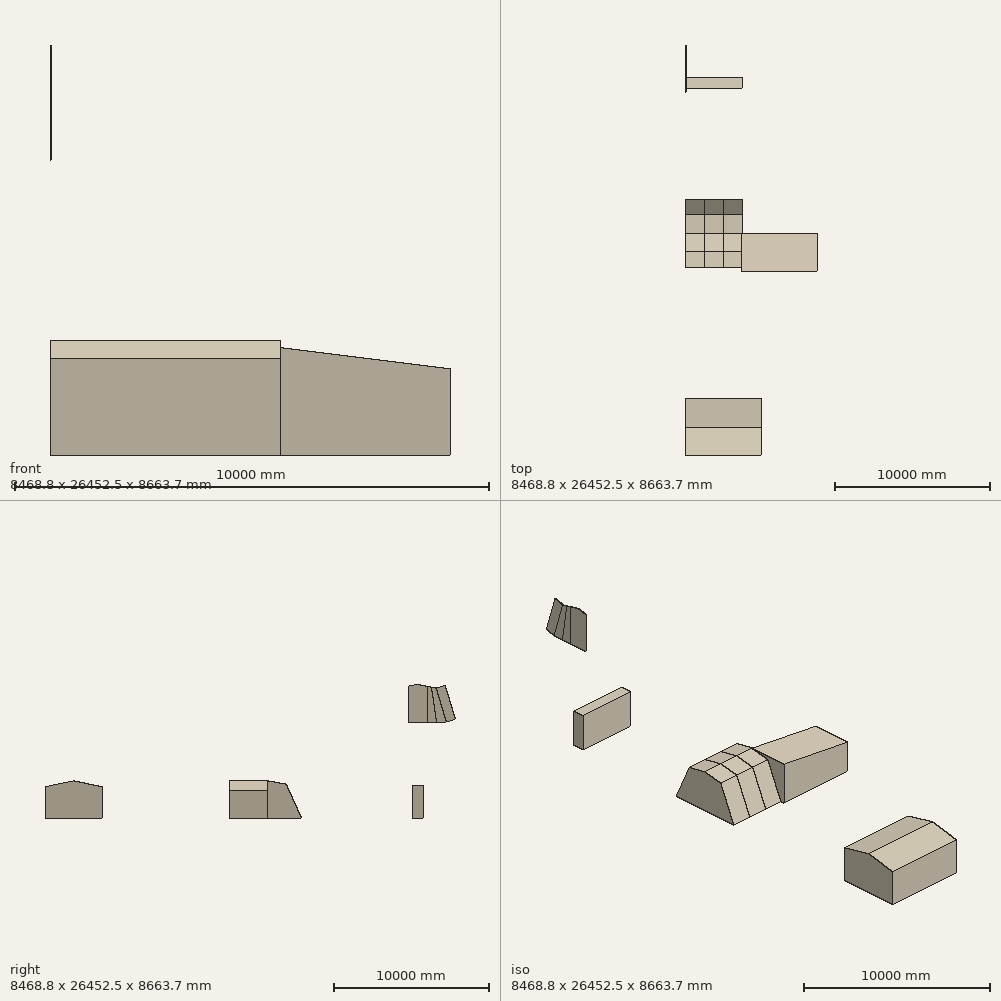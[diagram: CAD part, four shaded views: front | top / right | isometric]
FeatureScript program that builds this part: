
annotation { "Feature Type Name" : "Feature", "Feature Type Description" : "" }
export const myFeature = defineFeature(function(context is Context, id is Id, definition is map)
    precondition{}
    {
        {
            var Q0;
            Q0=qCreatedBy(makeId("Front.planeOp"),FACE);
            var sketch = newSketch(context, id + "F0", { "sketchPlane" : qUnion([Q0])});
            skLineSegment(sketch, "E0", {"start": v(3591.95, 0) * mm, "end": v(3591.95, 2438.4) * mm});
            skLineSegment(sketch, "E1", {"start": v(3591.95, 2438.4) * mm, "end": v(8468.75, 1828.8) * mm});
            skLineSegment(sketch, "E2", {"start": v(8468.75, 1828.8) * mm, "end": v(8468.75, 0) * mm});
            skLineSegment(sketch, "E3", {"start": v(8468.75, 0) * mm, "end": v(3591.95, 0) * mm});
            skSolve(sketch);
        }
        {
            var Q0;
            Q0=makeQuery(id+"F0.imprint","IMPRINT",FACE,{"disambiguationData":[TD([[makeQuery(id+"F0.imprint","IMPRINT",EDGE,{"derivedFrom":sQuery(id+"F0.wireOp",EDGE,"E0")}),-1.0]])]});
            extrude(context, id + "F1", {"entities" : qUnion([Q0]), "depth" : 2438.4 * mm});
        }
        {
            var Q0;
            Q0=qCreatedBy(makeId("Right.planeOp"),FACE);
            var sketch = newSketch(context, id + "F2", { "sketchPlane" : qUnion([Q0])});
            skLineSegment(sketch, "E4", {"start": v(-14333.51, 0) * mm, "end": v(-10675.91, 0) * mm});
            skLineSegment(sketch, "E5", {"start": v(-10675.91, 0) * mm, "end": v(-10675.91, 2057.4) * mm});
            skLineSegment(sketch, "E6", {"start": v(-10675.91, 2057.4) * mm, "end": v(-12504.71, 2438.4) * mm});
            skLineSegment(sketch, "E7", {"start": v(-12504.71, 2438.4) * mm, "end": v(-14333.51, 2057.4) * mm});
            skLineSegment(sketch, "E8", {"start": v(-14333.51, 2057.4) * mm, "end": v(-14333.51, 0) * mm});
            skLineSegment(sketch, "E9", {"start": v(2202.6, 0) * mm, "end": v(0, 0) * mm});
            skLineSegment(sketch, "E10", {"start": v(0, 0) * mm, "end": v(0, 2438.4) * mm, "construction": true});
            skLineSegment(sketch, "E11", {"start": v(0, 2438.4) * mm, "end": v(1199.97, 2222.73) * mm});
            skLineSegment(sketch, "E12", {"start": v(1199.97, 2222.73) * mm, "end": v(2202.6, 0) * mm});
            skLineSegment(sketch, "E13", {"start": v(711.2, 0) * mm, "end": v(711.2, 2310.57) * mm, "construction": true});
            skLineSegment(sketch, "E14", {"start": v(711.2, 2310.57) * mm, "end": v(711.2, 3306.28) * mm, "construction": true});
            skLineSegment(sketch, "E15", {"start": v(711.2, 3306.28) * mm, "end": v(1199.97, 2222.73) * mm, "construction": true});
            skLineSegment(sketch, "E16", {"start": v(711.2, 3306.28) * mm, "end": v(1422.4, 0) * mm, "construction": true});
            skLineSegment(sketch, "E17", {"start": v(711.2, 3306.28) * mm, "end": v(711.2, 3306.28) * mm});
            skLineSegment(sketch, "E18", {"start": v(1390.95, 146.22) * mm, "end": v(711.2, 0) * mm, "construction": true});
            skLineSegment(sketch, "E19", {"start": v(2070.7, 292.44) * mm, "end": v(1422.4, 0) * mm, "construction": true});
            skLineSegment(sketch, "E20", {"start": v(1390.95, 146.22) * mm, "end": v(711.2, 146.22) * mm, "construction": true});
            skLineSegment(sketch, "E21", {"start": v(2202.6, 5599.6) * mm, "end": v(0, 5599.6) * mm});
            skLineSegment(sketch, "E22", {"start": v(0, 5599.6) * mm, "end": v(0, 8038) * mm});
            skLineSegment(sketch, "E23", {"start": v(0, 8038) * mm, "end": v(1199.97, 7822.32) * mm});
            skLineSegment(sketch, "E24", {"start": v(1199.97, 7822.32) * mm, "end": v(2202.6, 5599.6) * mm});
            skLineSegment(sketch, "E25", {"start": v(711.2, 5599.6) * mm, "end": v(711.2, 7910.17) * mm});
            skLineSegment(sketch, "E26", {"start": v(711.2, 7910.17) * mm, "end": v(711.2, 8905.88) * mm, "construction": true});
            skLineSegment(sketch, "E27", {"start": v(711.2, 8905.88) * mm, "end": v(1199.97, 7822.32) * mm, "construction": true});
            skLineSegment(sketch, "E28", {"start": v(711.2, 8905.88) * mm, "end": v(1422.4, 5599.6) * mm, "construction": true});
            skLineSegment(sketch, "E29", {"start": v(711.2, 8905.88) * mm, "end": v(711.2, 8905.88) * mm});
            skLineSegment(sketch, "E30", {"start": v(1390.95, 5745.82) * mm, "end": v(711.2, 5599.6) * mm, "construction": true});
            skLineSegment(sketch, "E31", {"start": v(2070.7, 5892.03) * mm, "end": v(1422.4, 5599.6) * mm, "construction": true});
            skLineSegment(sketch, "E32", {"start": v(1390.95, 5745.82) * mm, "end": v(711.2, 5745.82) * mm, "construction": true});
            skLineSegment(sketch, "E33.MirrorCS", {"start": v(711.2, 8905.88) * mm, "end": v(0, 5599.6) * mm, "construction": true});
            skLineSegment(sketch, "E34", {"start": v(2070.7, 5892.03) * mm, "end": v(2202.6, 5599.6) * mm});
            skLineSegment(sketch, "E35", {"start": v(711.2, 5599.6) * mm, "end": v(711.2, 5278.79) * mm});
            skLineSegment(sketch, "E36", {"start": v(711.2, 5278.79) * mm, "end": v(0, 5599.6) * mm});
            skLineSegment(sketch, "E37", {"start": v(711.2, 7910.17) * mm, "end": v(934, 7870.13) * mm});
            skLineSegment(sketch, "E38.MirrorCS", {"start": v(711.2, 7910.17) * mm, "end": v(488.4, 7870.13) * mm});
            skLineSegment(sketch, "E39.left", {"start": v(711.2, 5278.79) * mm, "end": v(711.2, 7717.19) * mm});
            skLineSegment(sketch, "E40", {"start": v(711.2, 7717.19) * mm, "end": v(488.4, 7870.13) * mm});
            skLineSegment(sketch, "E41", {"start": v(488.4, 7870.13) * mm, "end": v(0, 5599.6) * mm});
            skLineSegment(sketch, "E42.MirrorCS", {"start": v(-711.2, 0) * mm, "end": v(-711.2, 2310.57) * mm, "construction": true});
            skLineSegment(sketch, "E43.MirrorCS", {"start": v(-2202.6, 0) * mm, "end": v(0, 0) * mm});
            skLineSegment(sketch, "E44.MirrorCS", {"start": v(-1390.95, 146.22) * mm, "end": v(-711.2, 0) * mm, "construction": true});
            skLineSegment(sketch, "E45.MirrorCS", {"start": v(-711.2, 3306.28) * mm, "end": v(-1422.4, 0) * mm, "construction": true});
            skLineSegment(sketch, "E46.MirrorCS", {"start": v(-711.2, 3306.28) * mm, "end": v(-1199.97, 2222.73) * mm, "construction": true});
            skLineSegment(sketch, "E47.MirrorCS", {"start": v(-1390.95, 146.22) * mm, "end": v(-711.2, 146.22) * mm, "construction": true});
            skLineSegment(sketch, "E48.MirrorCS", {"start": v(-1199.97, 2222.73) * mm, "end": v(-2202.6, 0) * mm});
            skLineSegment(sketch, "E49.MirrorCS", {"start": v(0, 2438.4) * mm, "end": v(-1199.97, 2222.73) * mm});
            skLineSegment(sketch, "E50.MirrorCS", {"start": v(-711.2, 2310.57) * mm, "end": v(-711.2, 3306.28) * mm, "construction": true});
            skLineSegment(sketch, "E51.MirrorCS", {"start": v(-2070.7, 292.44) * mm, "end": v(-1422.4, 0) * mm, "construction": true});
            skLineSegment(sketch, "E52.bottom", {"start": v(711.2, 5278.79) * mm, "end": v(101.6, 5278.79) * mm});
            skLineSegment(sketch, "E52.top", {"start": v(711.2, 7717.19) * mm, "end": v(101.6, 7717.19) * mm});
            skLineSegment(sketch, "E52.right", {"start": v(101.6, 5278.79) * mm, "end": v(101.6, 7717.19) * mm});
            skLineSegment(sketch, "E53", {"start": v(609.6, 0) * mm, "end": v(609.6, 2328.84) * mm, "construction": true});
            skLineSegment(sketch, "E54.MirrorCS", {"start": v(-609.6, 0) * mm, "end": v(-609.6, 2328.84) * mm, "construction": true});
            skLineSegment(sketch, "E55", {"start": v(11535.56, 0) * mm, "end": v(9679.38, 0) * mm});
            skLineSegment(sketch, "E56", {"start": v(9679.38, 0) * mm, "end": v(9679.38, 2438.4) * mm, "construction": true});
            skLineSegment(sketch, "E57", {"start": v(9679.38, 2438.4) * mm, "end": v(10872.53, 2187.74) * mm});
            skLineSegment(sketch, "E58", {"start": v(10872.53, 2187.74) * mm, "end": v(11535.56, 0) * mm});
            skLineSegment(sketch, "E59", {"start": v(10288.98, 0) * mm, "end": v(10288.98, 2310.33) * mm, "construction": true});
            skLineSegment(sketch, "E60", {"start": v(10288.98, 2310.33) * mm, "end": v(10288.98, 4113.24) * mm, "construction": true});
            skLineSegment(sketch, "E61", {"start": v(10288.98, 4113.24) * mm, "end": v(10872.53, 2187.74) * mm, "construction": true});
            skLineSegment(sketch, "E62", {"start": v(10288.98, 4113.24) * mm, "end": v(10898.58, 0) * mm, "construction": true});
            skLineSegment(sketch, "E63", {"start": v(10288.98, 4113.24) * mm, "end": v(10288.98, 4113.24) * mm});
            skLineSegment(sketch, "E64", {"start": v(10885.48, 88.4) * mm, "end": v(10288.98, 0) * mm, "construction": true});
            skLineSegment(sketch, "E65", {"start": v(11481.97, 176.8) * mm, "end": v(10898.58, 0) * mm, "construction": true});
            skLineSegment(sketch, "E66", {"start": v(10885.48, 88.4) * mm, "end": v(10288.98, 88.4) * mm, "construction": true});
            skLineSegment(sketch, "E67.MirrorCS", {"start": v(9069.78, 0) * mm, "end": v(9069.78, 2310.33) * mm, "construction": true});
            skLineSegment(sketch, "E68.MirrorCS", {"start": v(7823.2, 0) * mm, "end": v(9679.38, 0) * mm});
            skLineSegment(sketch, "E69.MirrorCS", {"start": v(8473.28, 88.4) * mm, "end": v(9069.78, 0) * mm, "construction": true});
            skLineSegment(sketch, "E70.MirrorCS", {"start": v(9069.78, 4113.24) * mm, "end": v(8460.18, 0) * mm, "construction": true});
            skLineSegment(sketch, "E71.MirrorCS", {"start": v(9069.78, 4113.24) * mm, "end": v(8486.22, 2187.74) * mm, "construction": true});
            skLineSegment(sketch, "E72.MirrorCS", {"start": v(8473.28, 88.4) * mm, "end": v(9069.78, 88.4) * mm, "construction": true});
            skLineSegment(sketch, "E73.MirrorCS", {"start": v(8486.22, 2187.74) * mm, "end": v(7823.2, 0) * mm});
            skLineSegment(sketch, "E74.MirrorCS", {"start": v(9679.38, 2438.4) * mm, "end": v(8486.22, 2187.74) * mm});
            skLineSegment(sketch, "E75.MirrorCS", {"start": v(9069.78, 2310.33) * mm, "end": v(9069.78, 4113.24) * mm, "construction": true});
            skLineSegment(sketch, "E76.MirrorCS", {"start": v(7876.78, 176.8) * mm, "end": v(8460.18, 0) * mm, "construction": true});
            skLineSegment(sketch, "E77", {"start": v(11535.56, 6225.26) * mm, "end": v(9679.38, 6225.26) * mm});
            skLineSegment(sketch, "E78", {"start": v(9679.38, 6225.26) * mm, "end": v(9679.38, 8663.66) * mm, "construction": true});
            skLineSegment(sketch, "E79", {"start": v(9679.38, 8663.66) * mm, "end": v(10872.53, 8413) * mm});
            skLineSegment(sketch, "E80", {"start": v(10872.53, 8413) * mm, "end": v(11535.56, 6225.26) * mm});
            skLineSegment(sketch, "E81", {"start": v(10288.98, 6225.26) * mm, "end": v(10288.98, 8535.6) * mm, "construction": true});
            skLineSegment(sketch, "E82", {"start": v(10288.98, 8535.6) * mm, "end": v(10288.98, 10338.5) * mm, "construction": true});
            skLineSegment(sketch, "E83", {"start": v(10288.98, 10338.5) * mm, "end": v(10872.53, 8413) * mm, "construction": true});
            skLineSegment(sketch, "E84", {"start": v(10288.98, 10338.5) * mm, "end": v(10898.58, 6225.26) * mm, "construction": true});
            skLineSegment(sketch, "E85", {"start": v(10885.48, 6313.67) * mm, "end": v(10288.98, 6225.26) * mm, "construction": true});
            skLineSegment(sketch, "E86", {"start": v(11481.97, 6402.07) * mm, "end": v(10898.58, 6225.26) * mm, "construction": true});
            skLineSegment(sketch, "E87", {"start": v(10885.48, 6313.67) * mm, "end": v(10288.98, 6313.67) * mm, "construction": true});
            skLineSegment(sketch, "E88.MirrorCS", {"start": v(9069.78, 6225.26) * mm, "end": v(9069.78, 8535.6) * mm, "construction": true});
            skLineSegment(sketch, "E89.MirrorCS", {"start": v(7823.2, 6225.26) * mm, "end": v(9679.38, 6225.26) * mm});
            skLineSegment(sketch, "E90.MirrorCS", {"start": v(8473.28, 6313.67) * mm, "end": v(9069.78, 6225.26) * mm, "construction": true});
            skLineSegment(sketch, "E91.MirrorCS", {"start": v(9069.78, 10338.5) * mm, "end": v(8460.18, 6225.26) * mm, "construction": true});
            skLineSegment(sketch, "E92.MirrorCS", {"start": v(9069.78, 10338.5) * mm, "end": v(8486.22, 8413) * mm, "construction": true});
            skLineSegment(sketch, "E93.MirrorCS", {"start": v(8473.28, 6313.67) * mm, "end": v(9069.78, 6313.67) * mm, "construction": true});
            skLineSegment(sketch, "E94.MirrorCS", {"start": v(8486.22, 8413) * mm, "end": v(7823.2, 6225.26) * mm});
            skLineSegment(sketch, "E95.MirrorCS", {"start": v(9679.38, 8663.66) * mm, "end": v(8486.22, 8413) * mm});
            skLineSegment(sketch, "E96.MirrorCS", {"start": v(9069.78, 8535.6) * mm, "end": v(9069.78, 10338.5) * mm, "construction": true});
            skLineSegment(sketch, "E97.MirrorCS", {"start": v(7876.78, 6402.07) * mm, "end": v(8460.18, 6225.26) * mm, "construction": true});
            skLineSegment(sketch, "E98", {"start": v(10288.98, 8535.6) * mm, "end": v(10564.76, 8477.66) * mm});
            skLineSegment(sketch, "E99", {"start": v(10564.76, 8477.66) * mm, "end": v(10872.53, 8413) * mm});
            skLineSegment(sketch, "E100.MirrorCS", {"start": v(10288.98, 10338.5) * mm, "end": v(9679.38, 6225.26) * mm, "construction": true});
            skLineSegment(sketch, "E101.MirrorCS", {"start": v(10288.98, 8535.6) * mm, "end": v(10013.2, 8477.66) * mm});
            skLineSegment(sketch, "E102", {"start": v(10013.2, 8477.66) * mm, "end": v(10288.98, 8326.52) * mm});
            skLineSegment(sketch, "E103.bottom", {"start": v(10288.98, 8326.52) * mm, "end": v(9679.38, 8326.52) * mm});
            skLineSegment(sketch, "E103.top", {"start": v(10288.98, 6040.52) * mm, "end": v(9679.38, 6040.52) * mm});
            skLineSegment(sketch, "E103.left", {"start": v(10288.98, 8326.52) * mm, "end": v(10288.98, 6040.52) * mm});
            skLineSegment(sketch, "E103.right", {"start": v(9679.38, 8326.52) * mm, "end": v(9679.38, 6040.52) * mm});
            skLineSegment(sketch, "E104", {"start": v(10013.2, 8477.66) * mm, "end": v(9679.38, 6225.26) * mm});
            skLineSegment(sketch, "E105", {"start": v(9679.38, 6225.26) * mm, "end": v(10288.98, 6040.52) * mm});
            skLineSegment(sketch, "E106", {"start": v(9069.78, 8535.6) * mm, "end": v(9069.78, 6225.26) * mm});
            skLineSegment(sketch, "E107", {"start": v(10564.76, 8477.66) * mm, "end": v(10898.58, 6225.26) * mm});
            skLineSegment(sketch, "E108", {"start": v(11535.56, 6225.26) * mm, "end": v(12118.96, 6402.07) * mm});
            skLineSegment(sketch, "E109", {"start": v(12118.96, 6402.07) * mm, "end": v(11455.93, 8589.8) * mm});
            skLineSegment(sketch, "E110", {"start": v(11455.93, 8589.8) * mm, "end": v(10872.53, 8413) * mm});
            skLineSegment(sketch, "E111", {"start": v(10288.98, 8535.6) * mm, "end": v(10288.98, 8326.52) * mm});
            skLineSegment(sketch, "E112", {"start": v(11535.56, 0) * mm, "end": v(12629.75, 331.6) * mm, "construction": true});
            skPoint(sketch, "E113", {"position": v(10564.76, 2252.4) * mm});
            skLineSegment(sketch, "E114", {"start": v(10564.76, 2252.4) * mm, "end": v(11824.6, 2634.2) * mm, "construction": true});
            skLineSegment(sketch, "E115", {"start": v(9679.38, 2438.4) * mm, "end": v(10177.45, 2438.4) * mm, "construction": true});
            skLineSegment(sketch, "E116.bottom", {"start": v(6237.45, 0) * mm, "end": v(6847.05, 0) * mm});
            skLineSegment(sketch, "E116.top", {"start": v(6237.45, 1701.8) * mm, "end": v(6847.05, 1701.8) * mm});
            skLineSegment(sketch, "E116.left", {"start": v(6237.45, 0) * mm, "end": v(6237.45, 1701.8) * mm});
            skLineSegment(sketch, "E116.right", {"start": v(6847.05, 0) * mm, "end": v(6847.05, 1701.8) * mm});
            skCircle(sketch, "E117", {"center": v(6542.25, 1816.1) * mm, "radius": 114.3 * mm});
            skLineSegment(sketch, "E118", {"start": v(6542.25, 1701.8) * mm, "end": v(6542.25, 1816.1) * mm});
            skLineSegment(sketch, "E119", {"start": v(10872.53, 2187.74) * mm, "end": v(10653.08, 2121.23) * mm, "construction": true});
            skLineSegment(sketch, "E120", {"start": v(10653.08, 2121.23) * mm, "end": v(10825.39, 1963.33) * mm, "construction": true});
            skLineSegment(sketch, "E121", {"start": v(10825.39, 1963.33) * mm, "end": v(10872.53, 2187.74) * mm, "construction": true});
            skLineSegment(sketch, "E122", {"start": v(10739.23, 2042.28) * mm, "end": v(10872.53, 2187.74) * mm, "construction": true});
            skPoint(sketch, "E123", {"position": v(8794, 2252.4) * mm});
            skLineSegment(sketch, "E124", {"start": v(8751.29, 0) * mm, "end": v(8751.29, 2461.36) * mm, "construction": true});
            skLineSegment(sketch, "E125", {"start": v(-13114.31, 0) * mm, "end": v(-13114.31, 2311.4) * mm, "construction": true});
            skLineSegment(sketch, "E126", {"start": v(-11895.11, 0) * mm, "end": v(-11895.11, 2311.4) * mm, "construction": true});
            skLineSegment(sketch, "E127", {"start": v(-12885.71, 0) * mm, "end": v(-12885.71, 1978.02) * mm, "construction": true});
            skLineSegment(sketch, "E128", {"start": v(-12885.71, 1978.02) * mm, "end": v(-12504.71, 2057.4) * mm, "construction": true});
            skLineSegment(sketch, "E129", {"start": v(-12504.71, 2057.4) * mm, "end": v(-12123.71, 1978.02) * mm, "construction": true});
            skLineSegment(sketch, "E130", {"start": v(-12123.71, 1978.02) * mm, "end": v(-12123.71, 0) * mm, "construction": true});
            skLineSegment(sketch, "E131", {"start": v(10034.98, 2133.6) * mm, "end": v(10034.98, 0) * mm});
            skLineSegment(sketch, "E132.MirrorCS", {"start": v(9323.78, 2133.6) * mm, "end": v(9323.78, 0) * mm});
            skLineSegment(sketch, "E133", {"start": v(9323.78, 2133.6) * mm, "end": v(10034.98, 2133.6) * mm});
            skSolve(sketch);
        }
        {
            var Q0;
            Q0=makeQuery(id+"F2.imprint","IMPRINT",FACE,{"disambiguationData":[TD([[makeQuery(id+"F2.imprint","IMPRINT",EDGE,{"derivedFrom":sQuery(id+"F2.wireOp",EDGE,"E4")}),1.0]])]});
            extrude(context, id + "F3", {"entities" : qUnion([Q0]), "depth" : 4876.8 * mm});
        }
        {
            var Q0;
            Q0=makeQuery(id+"F2.imprint","IMPRINT",FACE,{"disambiguationData":[TD([[makeQuery(id+"F2.imprint","IMPRINT",EDGE,{"derivedFrom":sQuery(id+"F2.wireOp",EDGE,"E9")}),-1.0]])]});
            extrude(context, id + "F4", {"entities" : qUnion([Q0]), "depth" : 1219.2 * mm});
        }
        {
            var Q0;
            Q0=makeQuery(id+"F4.opExtrude","CAP_FACE",FACE,{"disambiguationData":[OSD([sQuery(id+"F2.wireOp",EDGE,"E9"),sQuery(id+"F2.wireOp",EDGE,"E11"),sQuery(id+"F2.wireOp",EDGE,"E12"),sQuery(id+"F2.wireOp",EDGE,"E43.MirrorCS"),sQuery(id+"F2.wireOp",EDGE,"E48.MirrorCS"),sQuery(id+"F2.wireOp",EDGE,"E49.MirrorCS")])],"isStart":false});
            extrude(context, id + "F5", {"entities" : qUnion([Q0]), "depth" : 1219.2 * mm});
        }
        {
            var Q0;
            Q0=makeQuery(id+"F5.opExtrude","CAP_FACE",FACE,{"disambiguationData":[OSD([sQuery(id+"F2.wireOp",EDGE,"E9"),sQuery(id+"F2.wireOp",EDGE,"E11"),sQuery(id+"F2.wireOp",EDGE,"E12"),sQuery(id+"F2.wireOp",EDGE,"E43.MirrorCS"),sQuery(id+"F2.wireOp",EDGE,"E48.MirrorCS"),sQuery(id+"F2.wireOp",EDGE,"E49.MirrorCS")])],"isStart":false});
            extrude(context, id + "F6", {"entities" : qUnion([Q0]), "depth" : 1219.2 * mm});
        }
        {
            var Q0;
            Q0=makeQuery(id+"F2.imprint","IMPRINT",FACE,{"disambiguationData":[TD([[makeQuery(id+"F2.imprint","IMPRINT",EDGE,{"derivedFrom":sQuery(id+"F2.wireOp",EDGE,"E55")}),-1.0]])]});
            extrude(context, id + "F7", {"entities" : qUnion([Q0]), "depth" : 3657.6 * mm});
        }
        {
            var Q0;
            {var subQ0=sQuery(id+"F2.wireOp",EDGE,"E101.MirrorCS");Q0=makeQuery(id+"F2.imprint","IMPRINT",FACE,{"disambiguationData":[TD([[makeQuery(id+"F2.imprint","IMPRINT",EDGE,{"derivedFrom":subQ0}),-1.0]])]});}
            var Q1;
            Q1=makeQuery(id+"F2.imprint","IMPRINT",FACE,{"disambiguationData":[TD([[makeQuery(id+"F2.imprint","IMPRINT",EDGE,{"derivedFrom":sQuery(id+"F2.wireOp",EDGE,"E101.MirrorCS")}),1.0]])]});
            var Q2;
            {var subQ0=sQuery(id+"F2.wireOp",EDGE,"E102");Q2=makeQuery(id+"F2.imprint","IMPRINT",FACE,{"disambiguationData":[TD([[makeQuery(id+"F2.imprint","IMPRINT",EDGE,{"derivedFrom":subQ0}),-1.0]])]});}
            var Q3;
            {var subQ0=sQuery(id+"F2.wireOp",EDGE,"E103.right");var subQ1=sQuery(id+"F2.wireOp",EDGE,"E103.bottom");var subQ2=makeQuery(id+"F2.imprint","INTERSECT",VERTEX,{"derivedFrom":[subQ1,subQ0]});Q3=makeQuery(id+"F2.imprint","IMPRINT",FACE,{"disambiguationData":[TD([[makeQuery(id+"F2.imprint","IMPRINT",EDGE,{"disambiguationData":[TD([[subQ2,1.0]])],"derivedFrom":subQ1}),1.0]])]});}
            var Q4;
            {var subQ0=sQuery(id+"F2.wireOp",EDGE,"E104");var subQ5=sQuery(id+"F2.wireOp",EDGE,"E103.bottom");var subQ7=makeQuery(id+"F2.imprint","INTERSECT",VERTEX,{"derivedFrom":[subQ5,subQ0]});Q4=makeQuery(id+"F2.imprint","IMPRINT",FACE,{"disambiguationData":[TD([[makeQuery(id+"F2.imprint","IMPRINT",EDGE,{"disambiguationData":[TD([[subQ7,1.0]])],"derivedFrom":subQ5}),1.0]])]});}
            var Q5;
            {var subQ0=sQuery(id+"F2.wireOp",EDGE,"E80");Q5=makeQuery(id+"F2.imprint","IMPRINT",FACE,{"disambiguationData":[TD([[makeQuery(id+"F2.imprint","IMPRINT",EDGE,{"derivedFrom":subQ0}),-1.0]])]});}
            extrude(context, id + "F8", {"entities" : qUnion([Q0, Q1, Q2, Q3, Q4, Q5]), "depth" : 25.4 * mm});
        }
        {
            var Q0;
            {var subQ0=sQuery(id+"F2.wireOp",EDGE,"E107");Q0=makeQuery(id+"F2.imprint","IMPRINT",FACE,{"disambiguationData":[TD([[makeQuery(id+"F2.imprint","IMPRINT",EDGE,{"derivedFrom":subQ0}),-1.0]])]});}
            var Q1;
            Q1=makeQuery(id+"F2.imprint","IMPRINT",FACE,{"disambiguationData":[TD([[makeQuery(id+"F2.imprint","IMPRINT",EDGE,{"derivedFrom":sQuery(id+"F2.wireOp",EDGE,"E80")}),1.0]])]});
            extrude(context, id + "F9", {"entities" : qUnion([Q0, Q1]), "depth" : 25.4 * mm});
        }
        {
            var Q0;
            Q0=makeQuery(id+"F7.opExtrude","SWEPT_FACE",FACE,{"disambiguationData":[OSD([sQuery(id+"F2.wireOp",EDGE,"E55"),sQuery(id+"F2.wireOp",EDGE,"E68.MirrorCS")])]});
            shell(context, id + "F10", {"entities" : qUnion([Q0]), "thickness" : 25.4 * mm});
        }
        {
            var Q0;
            Q0=sQuery(id+"F2.wireOp",EDGE,"E58");
            var Q1;
            Q1=sQuery(id+"F2.wireOp",VERTEX,"E58.end");
            cPlane(context, id + "F11", {"entities" : qUnion([Q0, Q1]), "cplaneType" : CPlaneType.LINE_POINT, "offset" : 25.4 * mm, "width" : 152.4 * mm, "height" : 152.4 * mm});
        }
    });
